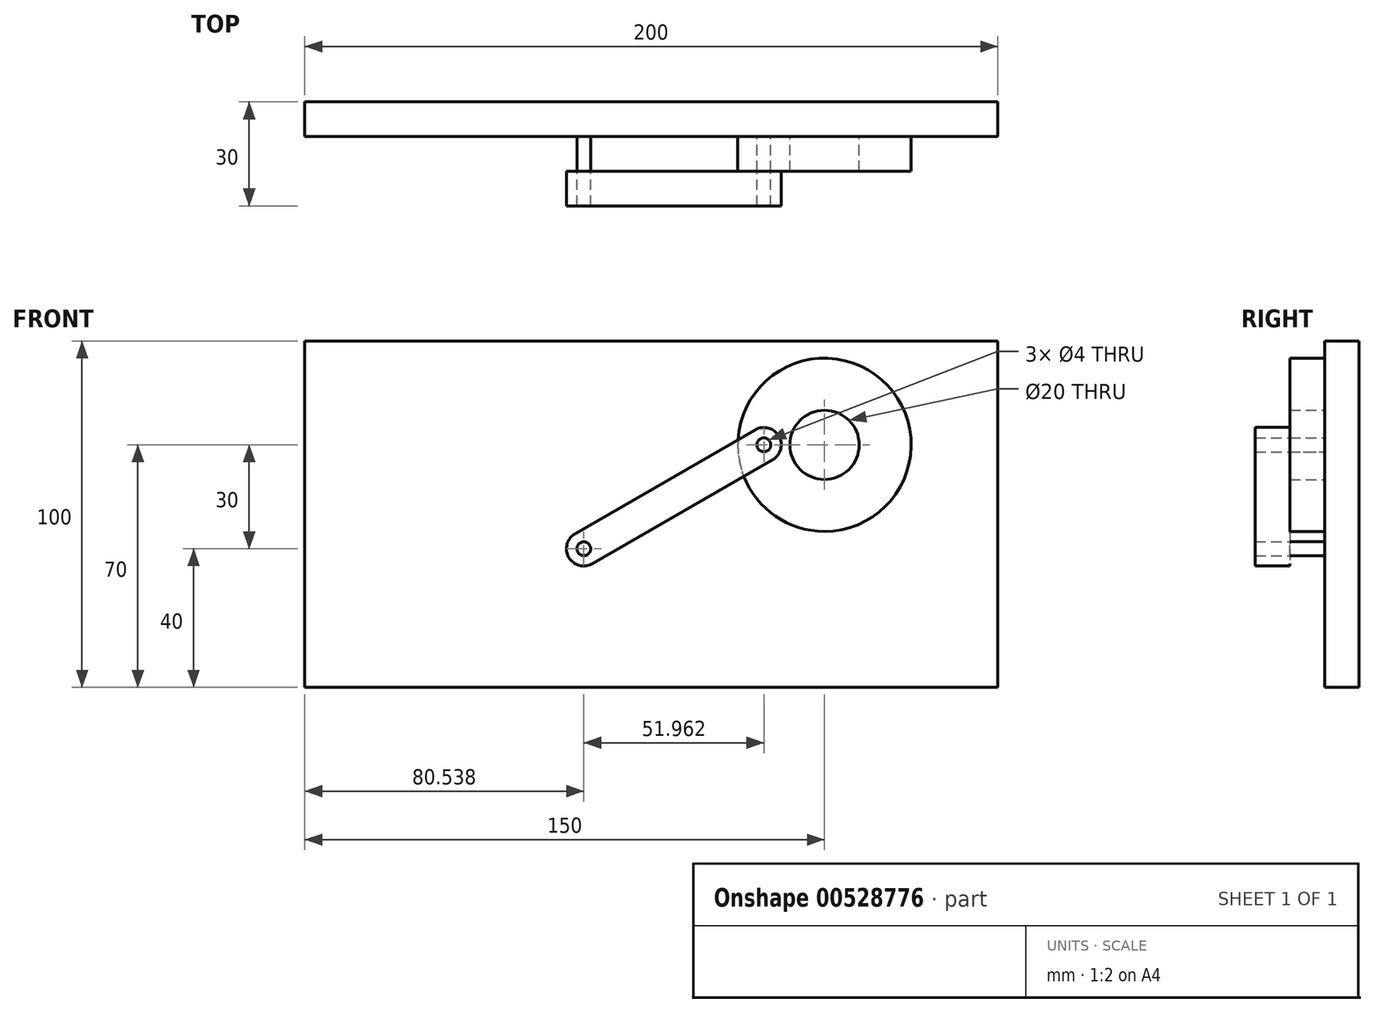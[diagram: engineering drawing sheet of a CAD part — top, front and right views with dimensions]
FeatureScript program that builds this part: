
annotation { "Feature Type Name" : "Feature", "Feature Type Description" : "" }
export const myFeature = defineFeature(function(context is Context, id is Id, definition is map)
    precondition{}
    {
        {
            var Q0;
            Q0=qCreatedBy(makeId("Front.planeOp"),FACE);
            var sketch = newSketch(context, id + "F0", { "sketchPlane" : qUnion([Q0])});
            skLineSegment(sketch, "E0.bottom", {"start": v(0, 0) * mm, "end": v(200, 0) * mm});
            skLineSegment(sketch, "E0.top", {"start": v(0, 100) * mm, "end": v(200, 100) * mm});
            skLineSegment(sketch, "E0.left", {"start": v(0, 0) * mm, "end": v(0, 100) * mm});
            skLineSegment(sketch, "E0.right", {"start": v(200, 0) * mm, "end": v(200, 100) * mm});
            skCircle(sketch, "E1", {"center": v(150, 70) * mm, "radius": 25 * mm});
            skCircle(sketch, "E2", {"center": v(132.5, 70) * mm, "radius": 5 * mm});
            skCircle(sketch, "E3", {"center": v(80.54, 40) * mm, "radius": 5 * mm});
            skLineSegment(sketch, "E4", {"start": v(78.04, 44.33) * mm, "end": v(130, 74.33) * mm});
            skLineSegment(sketch, "E5", {"start": v(83.04, 35.67) * mm, "end": v(135, 65.67) * mm});
            skCircle(sketch, "E6.0", {"center": v(150, 70) * mm, "radius": 10 * mm});
            skCircle(sketch, "E7.0", {"center": v(80.54, 40) * mm, "radius": 2 * mm});
            skCircle(sketch, "E8.0", {"center": v(132.5, 70) * mm, "radius": 2 * mm});
            skSolve(sketch);
        }
        {
            var Q0;
            Q0 = qSketchRegion(id + "F0", true);
            var Q1;
            Q1=makeQuery(id+"F0.imprint","IMPRINT",FACE,{"disambiguationData":[TD([[makeQuery(id+"F0.imprint","IMPRINT",EDGE,{"derivedFrom":sQuery(id+"F0.wireOp",EDGE,"E6.0")}),-1.0]])]});
            var Q2;
            {var subQ0=sQuery(id+"F0.wireOp",EDGE,"E4");var subQ1=sQuery(id+"F0.wireOp",EDGE,"E1");var subQ2=makeQuery(id+"F0.imprint","INTERSECT",VERTEX,{"derivedFrom":[subQ1,subQ0]});Q2=makeQuery(id+"F0.imprint","IMPRINT",FACE,{"disambiguationData":[TD([[makeQuery(id+"F0.imprint","IMPRINT",EDGE,{"disambiguationData":[TD([[subQ2,-1.0]])],"derivedFrom":subQ1}),-1.0]])]});}
            var Q3;
            {var subQ0=sQuery(id+"F0.wireOp",EDGE,"E3");var subQ1=makeQuery(id+"F0.imprint","INTERSECT",VERTEX,{"derivedFrom":[subQ0,sQuery(id+"F0.wireOp",EDGE,"E4")]});Q3=makeQuery(id+"F0.imprint","IMPRINT",FACE,{"disambiguationData":[TD([[makeQuery(id+"F0.imprint","IMPRINT",EDGE,{"disambiguationData":[TD([[subQ1,-1.0]])],"derivedFrom":subQ0}),1.0]])]});}
            var Q4;
            {var subQ0=sQuery(id+"F0.wireOp",EDGE,"E4");var subQ1=sQuery(id+"F0.wireOp",EDGE,"E1");var subQ2=makeQuery(id+"F0.imprint","INTERSECT",VERTEX,{"derivedFrom":[subQ1,subQ0]});Q4=makeQuery(id+"F0.imprint","IMPRINT",FACE,{"disambiguationData":[TD([[makeQuery(id+"F0.imprint","IMPRINT",EDGE,{"disambiguationData":[TD([[subQ2,-1.0]])],"derivedFrom":subQ1}),1.0]])]});}
            var Q5;
            Q5=makeQuery(id+"F0.imprint","IMPRINT",FACE,{"disambiguationData":[TD([[makeQuery(id+"F0.imprint","IMPRINT",EDGE,{"derivedFrom":sQuery(id+"F0.wireOp",EDGE,"E6.0")}),1.0]])]});
            var Q6;
            Q6=makeQuery(id+"F0.imprint","IMPRINT",FACE,{"disambiguationData":[TD([[makeQuery(id+"F0.imprint","IMPRINT",EDGE,{"derivedFrom":sQuery(id+"F0.wireOp",EDGE,"E7.0")}),1.0]])]});
            var Q7;
            Q7=makeQuery(id+"F0.imprint","IMPRINT",FACE,{"disambiguationData":[TD([[makeQuery(id+"F0.imprint","IMPRINT",EDGE,{"derivedFrom":sQuery(id+"F0.wireOp",EDGE,"E8.0")}),-1.0]])]});
            var Q8;
            Q8=makeQuery(id+"F0.imprint","IMPRINT",FACE,{"disambiguationData":[TD([[makeQuery(id+"F0.imprint","IMPRINT",EDGE,{"derivedFrom":sQuery(id+"F0.wireOp",EDGE,"E8.0")}),1.0]])]});
            extrude(context, id + "F1", {"entities" : qUnion([Q0, Q1, Q2, Q3, Q4, Q5, Q6, Q7, Q8]), "oppositeDirection" : true, "depth" : 10 * mm, "offsetDistance" : 25 * mm});
        }
        {
            var Q0;
            {var subQ0=sQuery(id+"F0.wireOp",EDGE,"E4");var subQ1=sQuery(id+"F0.wireOp",EDGE,"E1");var subQ2=makeQuery(id+"F0.imprint","INTERSECT",VERTEX,{"derivedFrom":[subQ1,subQ0]});Q0=makeQuery(id+"F0.imprint","IMPRINT",FACE,{"disambiguationData":[TD([[makeQuery(id+"F0.imprint","IMPRINT",EDGE,{"disambiguationData":[TD([[subQ2,-1.0]])],"derivedFrom":subQ1}),1.0]])]});}
            var Q1;
            {var subQ0=sQuery(id+"F0.wireOp",EDGE,"E2");var subQ1=makeQuery(id+"F0.imprint","INTERSECT",VERTEX,{"derivedFrom":[subQ0,sQuery(id+"F0.wireOp",EDGE,"E4")]});Q1=makeQuery(id+"F0.imprint","IMPRINT",FACE,{"disambiguationData":[TD([[makeQuery(id+"F0.imprint","IMPRINT",EDGE,{"disambiguationData":[TD([[subQ1,-1.0]])],"derivedFrom":subQ0}),1.0]])]});}
            var Q2;
            Q2=makeQuery(id+"F0.imprint","IMPRINT",FACE,{"disambiguationData":[TD([[makeQuery(id+"F0.imprint","IMPRINT",EDGE,{"derivedFrom":sQuery(id+"F0.wireOp",EDGE,"E6.0")}),-1.0]])]});
            extrude(context, id + "F2", {"entities" : qUnion([Q0, Q1, Q2]), "depth" : 10 * mm, "offsetDistance" : 25 * mm});
        }
        {
            var Q0;
            {var subQ0=sQuery(id+"F0.wireOp",EDGE,"E3");var subQ1=makeQuery(id+"F0.imprint","INTERSECT",VERTEX,{"derivedFrom":[subQ0,sQuery(id+"F0.wireOp",EDGE,"E4")]});Q0=makeQuery(id+"F0.imprint","IMPRINT",FACE,{"disambiguationData":[TD([[makeQuery(id+"F0.imprint","IMPRINT",EDGE,{"disambiguationData":[TD([[subQ1,-1.0]])],"derivedFrom":subQ0}),1.0]])]});}
            var Q1;
            {var subQ0=sQuery(id+"F0.wireOp",EDGE,"E4");var subQ1=sQuery(id+"F0.wireOp",EDGE,"E1");var subQ2=makeQuery(id+"F0.imprint","INTERSECT",VERTEX,{"derivedFrom":[subQ1,subQ0]});Q1=makeQuery(id+"F0.imprint","IMPRINT",FACE,{"disambiguationData":[TD([[makeQuery(id+"F0.imprint","IMPRINT",EDGE,{"disambiguationData":[TD([[subQ2,-1.0]])],"derivedFrom":subQ1}),-1.0]])]});}
            var Q2;
            {var subQ0=sQuery(id+"F0.wireOp",EDGE,"E2");var subQ1=makeQuery(id+"F0.imprint","INTERSECT",VERTEX,{"derivedFrom":[subQ0,sQuery(id+"F0.wireOp",EDGE,"E4")]});Q2=makeQuery(id+"F0.imprint","IMPRINT",FACE,{"disambiguationData":[TD([[makeQuery(id+"F0.imprint","IMPRINT",EDGE,{"disambiguationData":[TD([[subQ1,-1.0]])],"derivedFrom":subQ0}),1.0]])]});}
            var Q3;
            {var subQ0=sQuery(id+"F0.wireOp",EDGE,"E4");var subQ1=sQuery(id+"F0.wireOp",EDGE,"E1");var subQ2=makeQuery(id+"F0.imprint","INTERSECT",VERTEX,{"derivedFrom":[subQ1,subQ0]});Q3=makeQuery(id+"F0.imprint","IMPRINT",FACE,{"disambiguationData":[TD([[makeQuery(id+"F0.imprint","IMPRINT",EDGE,{"disambiguationData":[TD([[subQ2,-1.0]])],"derivedFrom":subQ1}),1.0]])]});}
            extrude(context, id + "F3", {"entities" : qUnion([Q0, Q1, Q2, Q3]), "depth" : 20 * mm, "offsetDistance" : 25 * mm, "hasSecondDirection" : true, "secondDirectionOppositeDirection" : false, "secondDirectionDepth" : 10 * mm});
        }
        {
            var Q0;
            Q0=makeQuery(id+"F0.imprint","IMPRINT",FACE,{"disambiguationData":[TD([[makeQuery(id+"F0.imprint","IMPRINT",EDGE,{"derivedFrom":sQuery(id+"F0.wireOp",EDGE,"E6.0")}),1.0]])]});
            extrude(context, id + "F4", {"entities" : qUnion([Q0]), "depth" : 10 * mm, "offsetDistance" : 25 * mm});
        }
        {
            var Q0;
            Q0=makeQuery(id+"F0.imprint","IMPRINT",FACE,{"disambiguationData":[TD([[makeQuery(id+"F0.imprint","IMPRINT",EDGE,{"derivedFrom":sQuery(id+"F0.wireOp",EDGE,"E7.0")}),1.0]])]});
            extrude(context, id + "F5", {"entities" : qUnion([Q0]), "depth" : 20 * mm, "offsetDistance" : 25 * mm});
        }
        {
            var Q0;
            Q0=makeQuery(id+"F0.imprint","IMPRINT",FACE,{"disambiguationData":[TD([[makeQuery(id+"F0.imprint","IMPRINT",EDGE,{"derivedFrom":sQuery(id+"F0.wireOp",EDGE,"E8.0")}),1.0]])]});
            extrude(context, id + "F6", {"entities" : qUnion([Q0]), "depth" : 20 * mm, "offsetDistance" : 25 * mm});
        }
    });
